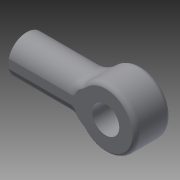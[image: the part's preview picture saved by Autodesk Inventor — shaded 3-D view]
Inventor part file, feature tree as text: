
AUTODESK INVENTOR PART (.ipt)
format: ipt  version: 2014 (Build 180170000, 170)  size: 247,808 bytes
history: native  units: mm
features: extrude x3, sketch x3, fillet x2, other x1
ambient origin geometry x8: Origin, YZ Plane, XZ Plane, XY Plane, X Axis, Y Axis, Z Axis, Center Point
bodies: Body1 (feature_tree)
feature tree (9):
  other  "ソリッド1"
  extrude  "押し出し1"  Depth=4.0mm
  extrude  "押し出し2"  Depth=1.4mm
  fillet  "フィレット1"  Radius=15.0mm
  fillet  "フィレット2"  Radius=5.0mm
  extrude  "押し出し3"  Depth=3.0mm
  sketch  "スケッチ1"
  sketch  "スケッチ2"
  sketch  "スケッチ3"
